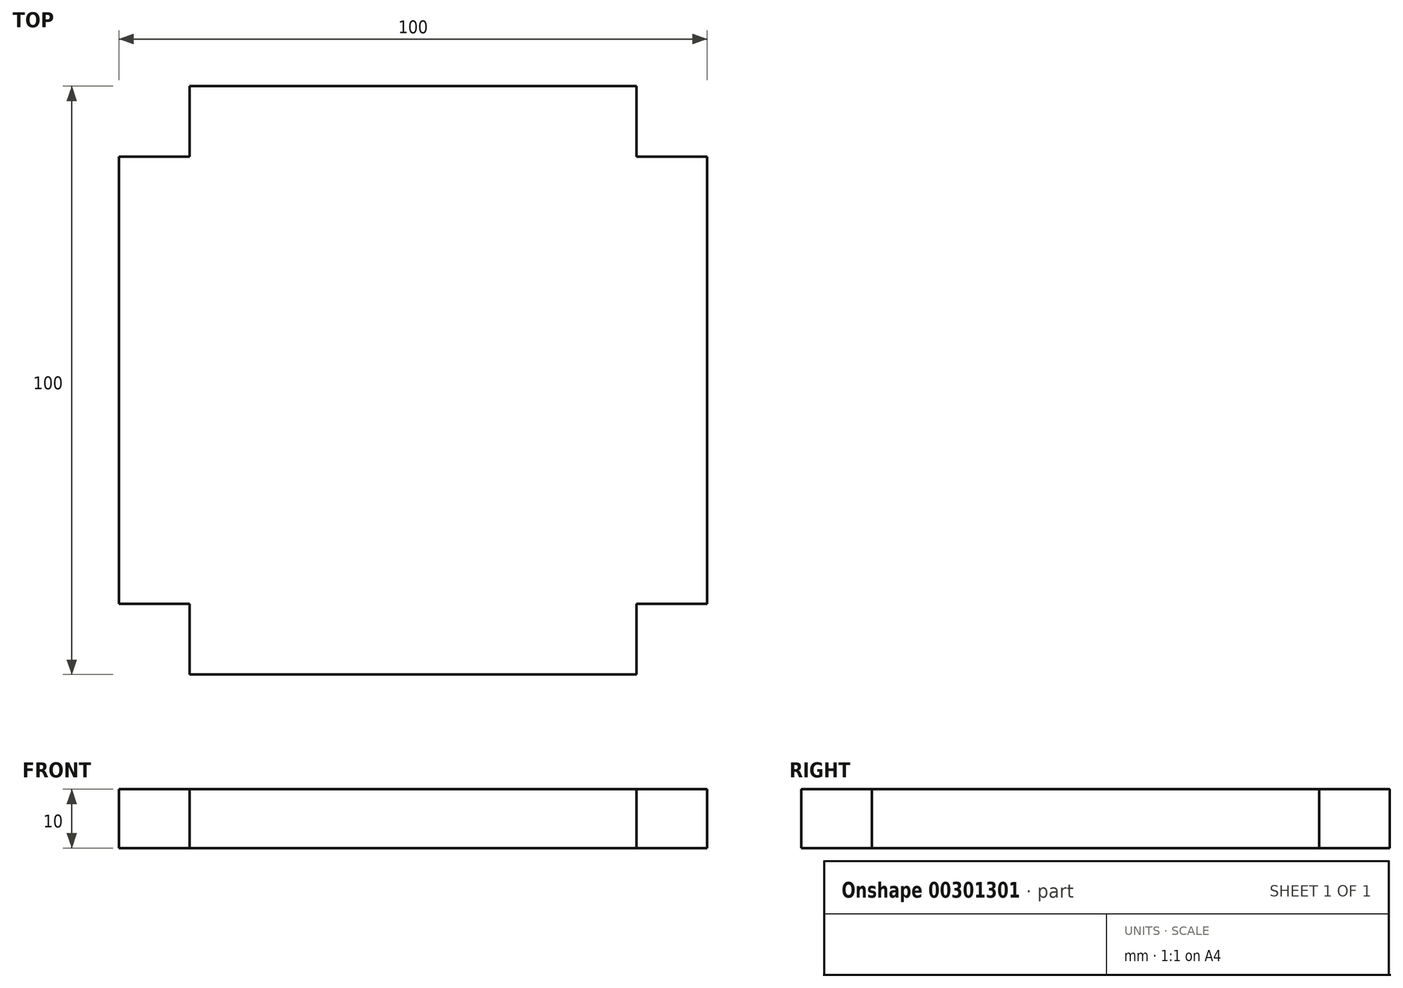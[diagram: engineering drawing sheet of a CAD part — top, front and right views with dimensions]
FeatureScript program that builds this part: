
annotation { "Feature Type Name" : "Feature", "Feature Type Description" : "" }
export const myFeature = defineFeature(function(context is Context, id is Id, definition is map)
    precondition{}
    {
        {
            var Q0;
            Q0=qCreatedBy(makeId("Top.planeOp"),FACE);
            var sketch = newSketch(context, id + "F0", { "sketchPlane" : qUnion([Q0])});
            skLineSegment(sketch, "E0.bottom", {"start": v(0, 0) * mm, "end": v(500, 0) * mm});
            skLineSegment(sketch, "E0.top", {"start": v(0, -500) * mm, "end": v(500, -500) * mm});
            skLineSegment(sketch, "E0.left", {"start": v(0, 0) * mm, "end": v(0, -500) * mm});
            skLineSegment(sketch, "E0.right", {"start": v(500, 0) * mm, "end": v(500, -500) * mm});
            skSolve(sketch);
        }
        {
            var Q0;
            Q0=makeQuery(id+"F0.imprint","IMPRINT",FACE,{"disambiguationData":[TD([[makeQuery(id+"F0.imprint","IMPRINT",EDGE,{"derivedFrom":sQuery(id+"F0.wireOp",EDGE,"E0.bottom")}),-1.0]])]});
            extrude(context, id + "F1", {"entities" : qUnion([Q0]), "depth" : 50 * mm});
        }
        {
            var Q0;
            Q0=makeQuery(id+"F1.opExtrude","CAP_FACE",FACE,{"disambiguationData":[OSD([sQuery(id+"F0.wireOp",EDGE,"E0.bottom"),sQuery(id+"F0.wireOp",EDGE,"E0.top"),sQuery(id+"F0.wireOp",EDGE,"E0.left"),sQuery(id+"F0.wireOp",EDGE,"E0.right")])],"isStart":false});
            var sketch = newSketch(context, id + "F2", { "sketchPlane" : qUnion([Q0])});
            skLineSegment(sketch, "E1.bottom", {"start": v(440, -440) * mm, "end": v(500, -440) * mm});
            skLineSegment(sketch, "E1.top", {"start": v(440, -500) * mm, "end": v(500, -500) * mm});
            skLineSegment(sketch, "E1.left", {"start": v(440, -440) * mm, "end": v(440, -500) * mm});
            skLineSegment(sketch, "E1.right", {"start": v(500, -440) * mm, "end": v(500, -500) * mm});
            skLineSegment(sketch, "E2.bottom", {"start": v(0, 0) * mm, "end": v(60, 0) * mm});
            skLineSegment(sketch, "E2.top", {"start": v(0, -60) * mm, "end": v(60, -60) * mm});
            skLineSegment(sketch, "E2.left", {"start": v(0, 0) * mm, "end": v(0, -60) * mm});
            skLineSegment(sketch, "E2.right", {"start": v(60, 0) * mm, "end": v(60, -60) * mm});
            skLineSegment(sketch, "E3.bottom", {"start": v(500, 0) * mm, "end": v(440, 0) * mm});
            skLineSegment(sketch, "E3.top", {"start": v(500, -60) * mm, "end": v(440, -60) * mm});
            skLineSegment(sketch, "E3.left", {"start": v(500, 0) * mm, "end": v(500, -60) * mm});
            skLineSegment(sketch, "E3.right", {"start": v(440, 0) * mm, "end": v(440, -60) * mm});
            skLineSegment(sketch, "E4.bottom", {"start": v(0, -500) * mm, "end": v(60, -500) * mm});
            skLineSegment(sketch, "E4.top", {"start": v(0, -440) * mm, "end": v(60, -440) * mm});
            skLineSegment(sketch, "E4.left", {"start": v(0, -500) * mm, "end": v(0, -440) * mm});
            skLineSegment(sketch, "E4.right", {"start": v(60, -500) * mm, "end": v(60, -440) * mm});
            skSolve(sketch);
        }
        {
            var Q0;
            Q0=makeQuery(id+"F2.imprint","IMPRINT",FACE,{"disambiguationData":[TD([[makeQuery(id+"F2.imprint","IMPRINT",EDGE,{"derivedFrom":sQuery(id+"F2.wireOp",EDGE,"E1.bottom")}),-1.0]])]});
            var Q1;
            Q1=makeQuery(id+"F2.imprint","IMPRINT",FACE,{"disambiguationData":[TD([[makeQuery(id+"F2.imprint","IMPRINT",EDGE,{"derivedFrom":sQuery(id+"F2.wireOp",EDGE,"E2.bottom")}),-1.0]])]});
            var Q2;
            Q2=makeQuery(id+"F2.imprint","IMPRINT",FACE,{"disambiguationData":[TD([[makeQuery(id+"F2.imprint","IMPRINT",EDGE,{"derivedFrom":sQuery(id+"F2.wireOp",EDGE,"E4.bottom")}),1.0]])]});
            var Q3;
            Q3=makeQuery(id+"F2.imprint","IMPRINT",FACE,{"disambiguationData":[TD([[makeQuery(id+"F2.imprint","IMPRINT",EDGE,{"derivedFrom":sQuery(id+"F2.wireOp",EDGE,"E3.bottom")}),-1.0]])]});
            extrude(context, id + "F3", {"entities" : qUnion([Q0, Q1, Q2, Q3]), "operationType" : NewBodyOperationType.REMOVE, "oppositeDirection" : true, "depth" : 90 * mm});
        }
        {
            var Q0;
            Q0=makeQuery(id+"F1.opExtrude","SWEPT_BODY",BODY,{"disambiguationData":[OSD([sQuery(id+"F0.wireOp",EDGE,"E0.bottom"),sQuery(id+"F0.wireOp",EDGE,"E0.top"),sQuery(id+"F0.wireOp",EDGE,"E0.left"),sQuery(id+"F0.wireOp",EDGE,"E0.right")])]});
            var Q1;
            Q1=qCreatedBy(makeId("Origin.pointOp"),VERTEX);
            transform(context, id + "F4", {"entities" : qUnion([Q0]), "transformType" : TransformType.SCALE_UNIFORMLY, "scale" : 0.2, "scalePoint" : qUnion([Q1]), "makeCopy" : false});
        }
    });
